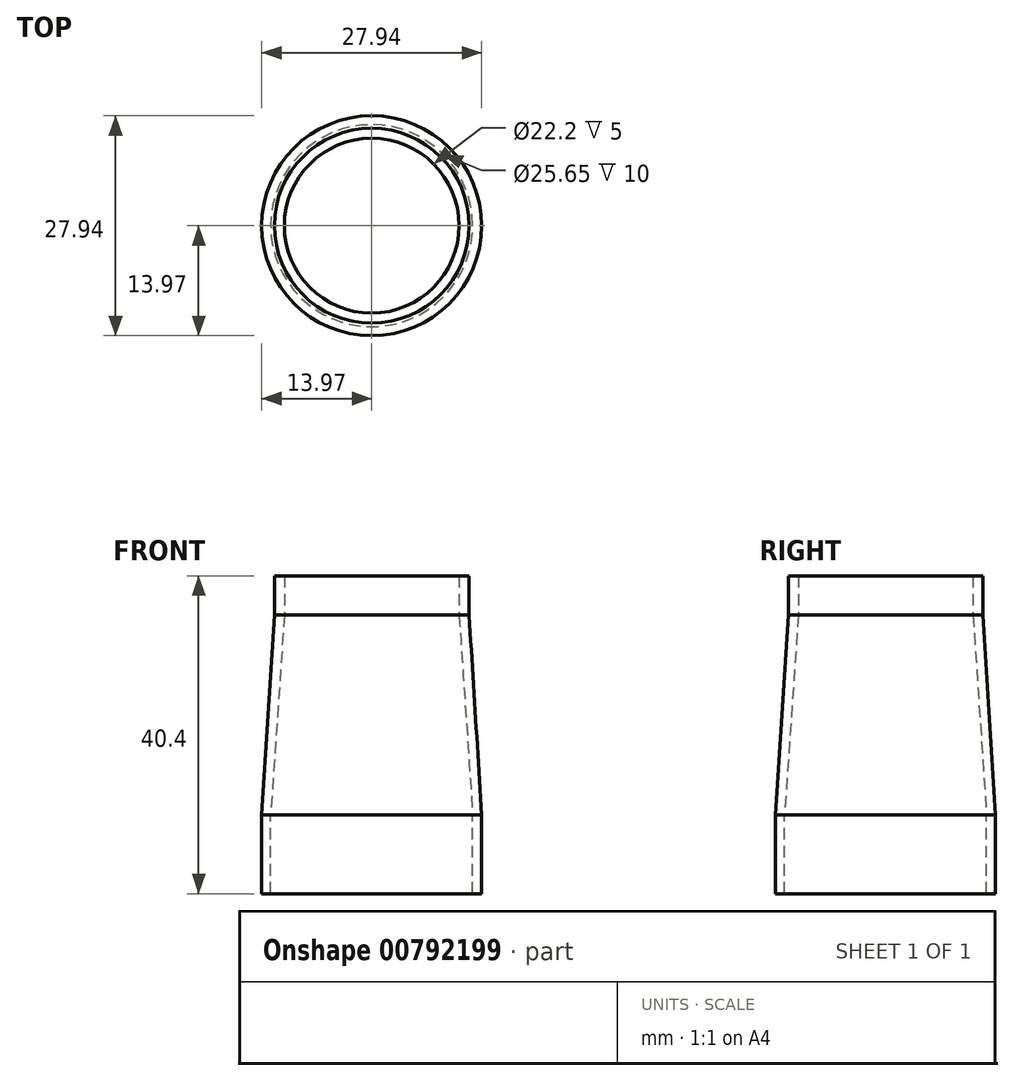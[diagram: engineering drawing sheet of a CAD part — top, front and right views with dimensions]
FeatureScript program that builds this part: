
annotation { "Feature Type Name" : "Feature", "Feature Type Description" : "" }
export const myFeature = defineFeature(function(context is Context, id is Id, definition is map)
    precondition{}
    {
        {
            var Q0;
            Q0=qCreatedBy(makeId("Top.planeOp"),FACE);
            cPlane(context, id + "F0", {"entities" : qUnion([Q0]), "cplaneType" : CPlaneType.OFFSET, "offset" : 25.4 * mm, "width" : 152.4 * mm, "height" : 152.4 * mm});
        }
        {
            var Q0;
            Q0=qCreatedBy(id+"F0.planeOp",FACE);
            var sketch = newSketch(context, id + "F1", { "sketchPlane" : qUnion([Q0])});
            skPoint(sketch, "E0.center.orphan", {"position": v(0, -6.74) * mm});
            skCircle(sketch, "E1", {"center": v(0, 0) * mm, "radius": 11.1 * mm});
            skSolve(sketch);
        }
        {
            var Q0;
            Q0=qCreatedBy(makeId("Top.planeOp"),FACE);
            var sketch = newSketch(context, id + "F2", { "sketchPlane" : qUnion([Q0])});
            skCircle(sketch, "E2", {"center": v(0, 0) * mm, "radius": 12.83 * mm});
            skSolve(sketch);
        }
        {
            var Q0;
            Q0=qCreatedBy(id+"F0.planeOp",FACE);
            var sketch = newSketch(context, id + "F3", { "sketchPlane" : qUnion([Q0])});
            skCircle(sketch, "E3", {"center": v(0, 0) * mm, "radius": 12.37 * mm});
            skSolve(sketch);
        }
        {
            var Q0;
            Q0=qCreatedBy(makeId("Top.planeOp"),FACE);
            var sketch = newSketch(context, id + "F4", { "sketchPlane" : qUnion([Q0])});
            skCircle(sketch, "E4.0", {"center": v(0, 0) * mm, "radius": 13.97 * mm});
            skSolve(sketch);
        }
        {
            var Q0;
            Q0=makeQuery(id+"F3.imprint","IMPRINT",FACE,{"disambiguationData":[TD([[makeQuery(id+"F3.imprint","IMPRINT",EDGE,{"derivedFrom":sQuery(id+"F3.wireOp",EDGE,"E3")}),1.0]])]});
            var Q1;
            Q1=makeQuery(id+"F4.imprint","IMPRINT",FACE,{"disambiguationData":[TD([[makeQuery(id+"F4.imprint","IMPRINT",EDGE,{"derivedFrom":sQuery(id+"F4.wireOp",EDGE,"E4.0")}),1.0]])]});
            loft(context, id + "F5", {"sheetProfilesArray" : [{ "sheetProfileEntities" : qUnion([Q0]) }, { "sheetProfileEntities" : qUnion([Q1]) }]});
        }
        {
            var Q1;
            Q1=makeQuery(id+"F1.imprint","IMPRINT",FACE,{"disambiguationData":[TD([[makeQuery(id+"F1.imprint","IMPRINT",EDGE,{"derivedFrom":sQuery(id+"F1.wireOp",EDGE,"E1")}),1.0]])]});
            var Q2;
            Q2=makeQuery(id+"F2.imprint","IMPRINT",FACE,{"disambiguationData":[TD([[makeQuery(id+"F2.imprint","IMPRINT",EDGE,{"derivedFrom":sQuery(id+"F2.wireOp",EDGE,"E2")}),1.0]])]});
            loft(context, id + "F6", {"operationType" : NewBodyOperationType.REMOVE, "sheetProfilesArray" : [{ "sheetProfileEntities" : qUnion([Q1]) }, { "sheetProfileEntities" : qUnion([Q2]) }]});
        }
        {
            var Q0;
            Q0 = qSketchRegion(id + "F3", true);
            extrude(context, id + "F7", {"entities" : qUnion([Q0]), "operationType" : NewBodyOperationType.ADD, "depth" : 5 * mm, "offsetDistance" : 25.4 * mm});
        }
        {
            var Q0;
            Q0 = qSketchRegion(id + "F1", true);
            extrude(context, id + "F8", {"entities" : qUnion([Q0]), "operationType" : NewBodyOperationType.REMOVE, "depth" : 25.4 * mm, "offsetDistance" : 25.4 * mm});
        }
        {
            var Q0;
            Q0 = qSketchRegion(id + "F4", true);
            extrude(context, id + "F9", {"entities" : qUnion([Q0]), "operationType" : NewBodyOperationType.ADD, "oppositeDirection" : true, "depth" : 10 * mm, "offsetDistance" : 25.4 * mm});
        }
        {
            var Q0;
            Q0 = qSketchRegion(id + "F2", true);
            extrude(context, id + "F10", {"entities" : qUnion([Q0]), "operationType" : NewBodyOperationType.REMOVE, "oppositeDirection" : true, "depth" : 25.4 * mm, "offsetDistance" : 25.4 * mm});
        }
    });
